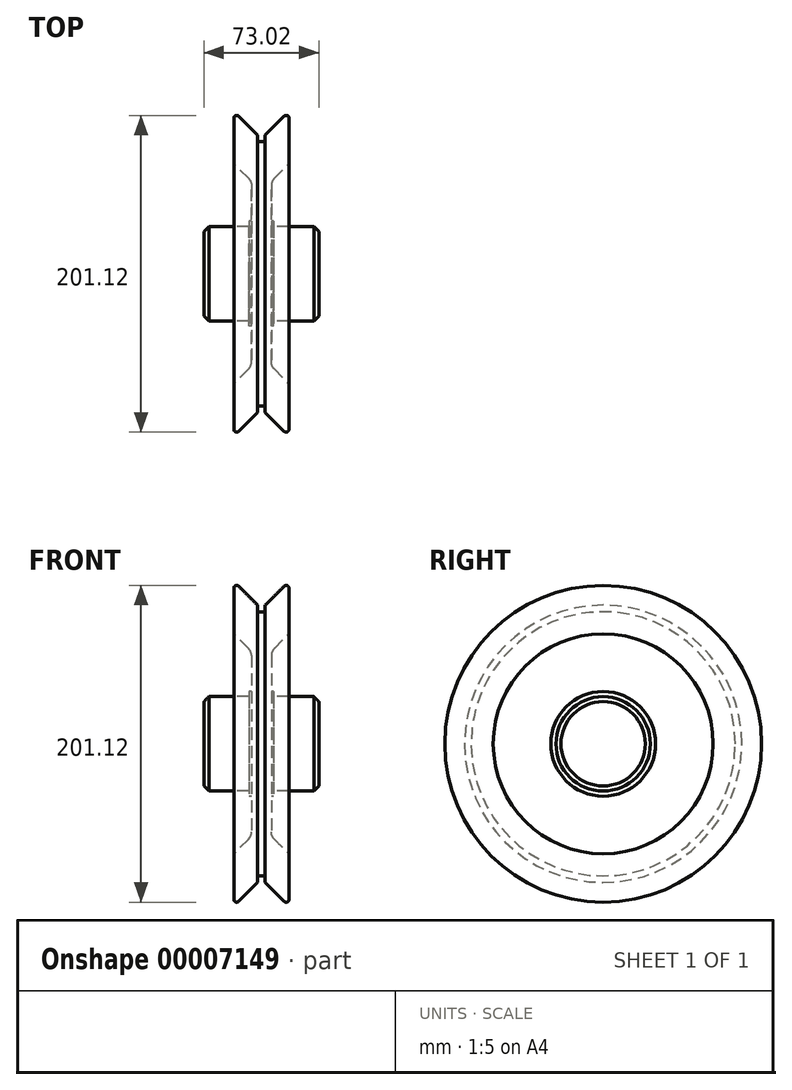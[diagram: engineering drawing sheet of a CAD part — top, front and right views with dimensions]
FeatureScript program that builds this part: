
annotation { "Feature Type Name" : "Feature", "Feature Type Description" : "" }
export const myFeature = defineFeature(function(context is Context, id is Id, definition is map)
    precondition{}
    {
        {
            var Q0;
            Q0=qCreatedBy(makeId("Front.planeOp"),FACE);
            var sketch = newSketch(context, id + "F0", { "sketchPlane" : qUnion([Q0])});
            skLineSegment(sketch, "E0", {"start": v(36.51, 0) * mm, "end": v(36.51, 29.97) * mm});
            skLineSegment(sketch, "E1", {"start": v(36.51, 29.97) * mm, "end": v(7.84, 29.97) * mm});
            skLineSegment(sketch, "E2", {"start": v(7.84, 29.97) * mm, "end": v(7.84, 33.27) * mm});
            skLineSegment(sketch, "E3", {"start": v(7.84, 33.27) * mm, "end": v(6.34, 33.27) * mm});
            skLineSegment(sketch, "E4", {"start": v(6.34, 33.27) * mm, "end": v(6.34, 58.72) * mm});
            skLineSegment(sketch, "E5", {"start": v(6.34, 58.72) * mm, "end": v(17.46, 69.85) * mm});
            skLineSegment(sketch, "E6", {"start": v(17.46, 69.85) * mm, "end": v(17.46, 100.56) * mm});
            skLineSegment(sketch, "E7", {"start": v(17.46, 100.56) * mm, "end": v(14.9, 100.56) * mm});
            skLineSegment(sketch, "E8", {"start": v(14.9, 100.56) * mm, "end": v(2.39, 88.05) * mm});
            skCircle(sketch, "E9", {"center": v(0, 94.39) * mm, "radius": 6.17 * mm, "construction": true});
            skLineSegment(sketch, "E10", {"start": v(2.39, 88.05) * mm, "end": v(2.39, 83.9) * mm});
            skLineSegment(sketch, "E11", {"start": v(2.39, 83.9) * mm, "end": v(0, 83.9) * mm});
            skLineSegment(sketch, "E12.0.MirrorCS", {"start": v(-2.39, 83.9) * mm, "end": v(0, 83.9) * mm});
            skLineSegment(sketch, "E13.0.MirrorCS", {"start": v(-2.39, 88.05) * mm, "end": v(-2.39, 83.9) * mm});
            skLineSegment(sketch, "E14.0.MirrorCS", {"start": v(-14.9, 100.56) * mm, "end": v(-2.39, 88.05) * mm});
            skLineSegment(sketch, "E15.0.MirrorCS", {"start": v(-17.46, 100.56) * mm, "end": v(-14.9, 100.56) * mm});
            skLineSegment(sketch, "E16.0.MirrorCS", {"start": v(-17.46, 69.85) * mm, "end": v(-17.46, 100.56) * mm});
            skLineSegment(sketch, "E17.0.MirrorCS", {"start": v(-6.34, 58.72) * mm, "end": v(-17.46, 69.85) * mm});
            skLineSegment(sketch, "E18.0.MirrorCS", {"start": v(-6.34, 33.27) * mm, "end": v(-6.34, 58.72) * mm});
            skLineSegment(sketch, "E19.0.MirrorCS", {"start": v(-7.84, 29.97) * mm, "end": v(-7.84, 33.27) * mm});
            skLineSegment(sketch, "E20.0.MirrorCS", {"start": v(-7.84, 33.27) * mm, "end": v(-6.34, 33.27) * mm});
            skLineSegment(sketch, "E21.0.MirrorCS", {"start": v(-36.51, 29.97) * mm, "end": v(-7.84, 29.97) * mm});
            skLineSegment(sketch, "E22.0.MirrorCS", {"start": v(-36.51, 0) * mm, "end": v(-36.51, 29.97) * mm});
            skLineSegment(sketch, "E23", {"start": v(-36.51, 0) * mm, "end": v(36.51, 0) * mm});
            skSolve(sketch);
        }
        {
            var Q0;
            Q0=makeQuery(id+"F0.imprint","IMPRINT",FACE,{"disambiguationData":[TD([[makeQuery(id+"F0.imprint","IMPRINT",EDGE,{"derivedFrom":sQuery(id+"F0.wireOp",EDGE,"E0")}),1.0]])]});
            var Q1;
            Q1=sQuery(id+"F0.wireOp",EDGE,"E23");
            revolve(context, id + "F1", {"entities" : qUnion([Q0]), "axis" : qUnion([Q1]), "revolveType" : RevolveType.FULL});
        }
        {
            var Q0;
            Q0=makeQuery(id+"F1.opRevolve","SWEPT_EDGE",EDGE,{"disambiguationData":[OSD([sQuery(id+"F0.wireOp",EDGE,"E0"),sQuery(id+"F0.wireOp",EDGE,"E1")])]});
            var Q1;
            Q1=makeQuery(id+"F1.opRevolve","SWEPT_EDGE",EDGE,{"disambiguationData":[OSD([sQuery(id+"F0.wireOp",EDGE,"E21.0.MirrorCS"),sQuery(id+"F0.wireOp",EDGE,"E22.0.MirrorCS")])]});
            chamfer(context, id + "F2", {"entities" : qUnion([Q0, Q1]), "width" : 3.17 * mm, "tangentPropagation" : true});
        }
        {
            var Q0;
            Q0=makeQuery(id+"F1.opRevolve","SWEPT_EDGE",EDGE,{"disambiguationData":[OSD([sQuery(id+"F0.wireOp",EDGE,"E4"),sQuery(id+"F0.wireOp",EDGE,"E5")])]});
            var Q1;
            Q1=makeQuery(id+"F1.opRevolve","SWEPT_EDGE",EDGE,{"disambiguationData":[OSD([sQuery(id+"F0.wireOp",EDGE,"E17.0.MirrorCS"),sQuery(id+"F0.wireOp",EDGE,"E18.0.MirrorCS")])]});
            fillet(context, id + "F3", {"entities" : qUnion([Q0, Q1]), "radius" : 6.35 * mm, "tangentPropagation" : true, "allowEdgeOverflow" : false});
        }
        {
            var Q0;
            Q0=makeQuery(id+"F1.opRevolve","SWEPT_EDGE",EDGE,{"disambiguationData":[OSD([sQuery(id+"F0.wireOp",EDGE,"E14.0.MirrorCS"),sQuery(id+"F0.wireOp",EDGE,"E15.0.MirrorCS")])]});
            var Q1;
            Q1=makeQuery(id+"F1.opRevolve","SWEPT_EDGE",EDGE,{"disambiguationData":[OSD([sQuery(id+"F0.wireOp",EDGE,"E15.0.MirrorCS"),sQuery(id+"F0.wireOp",EDGE,"E16.0.MirrorCS")])]});
            var Q2;
            Q2=makeQuery(id+"F1.opRevolve","SWEPT_EDGE",EDGE,{"disambiguationData":[OSD([sQuery(id+"F0.wireOp",EDGE,"E7"),sQuery(id+"F0.wireOp",EDGE,"E8")])]});
            var Q3;
            Q3=makeQuery(id+"F1.opRevolve","SWEPT_EDGE",EDGE,{"disambiguationData":[OSD([sQuery(id+"F0.wireOp",EDGE,"E6"),sQuery(id+"F0.wireOp",EDGE,"E7")])]});
            fillet(context, id + "F4", {"entities" : qUnion([Q0, Q1, Q2, Q3]), "radius" : 1.52 * mm, "tangentPropagation" : true, "allowEdgeOverflow" : false});
        }
    });
